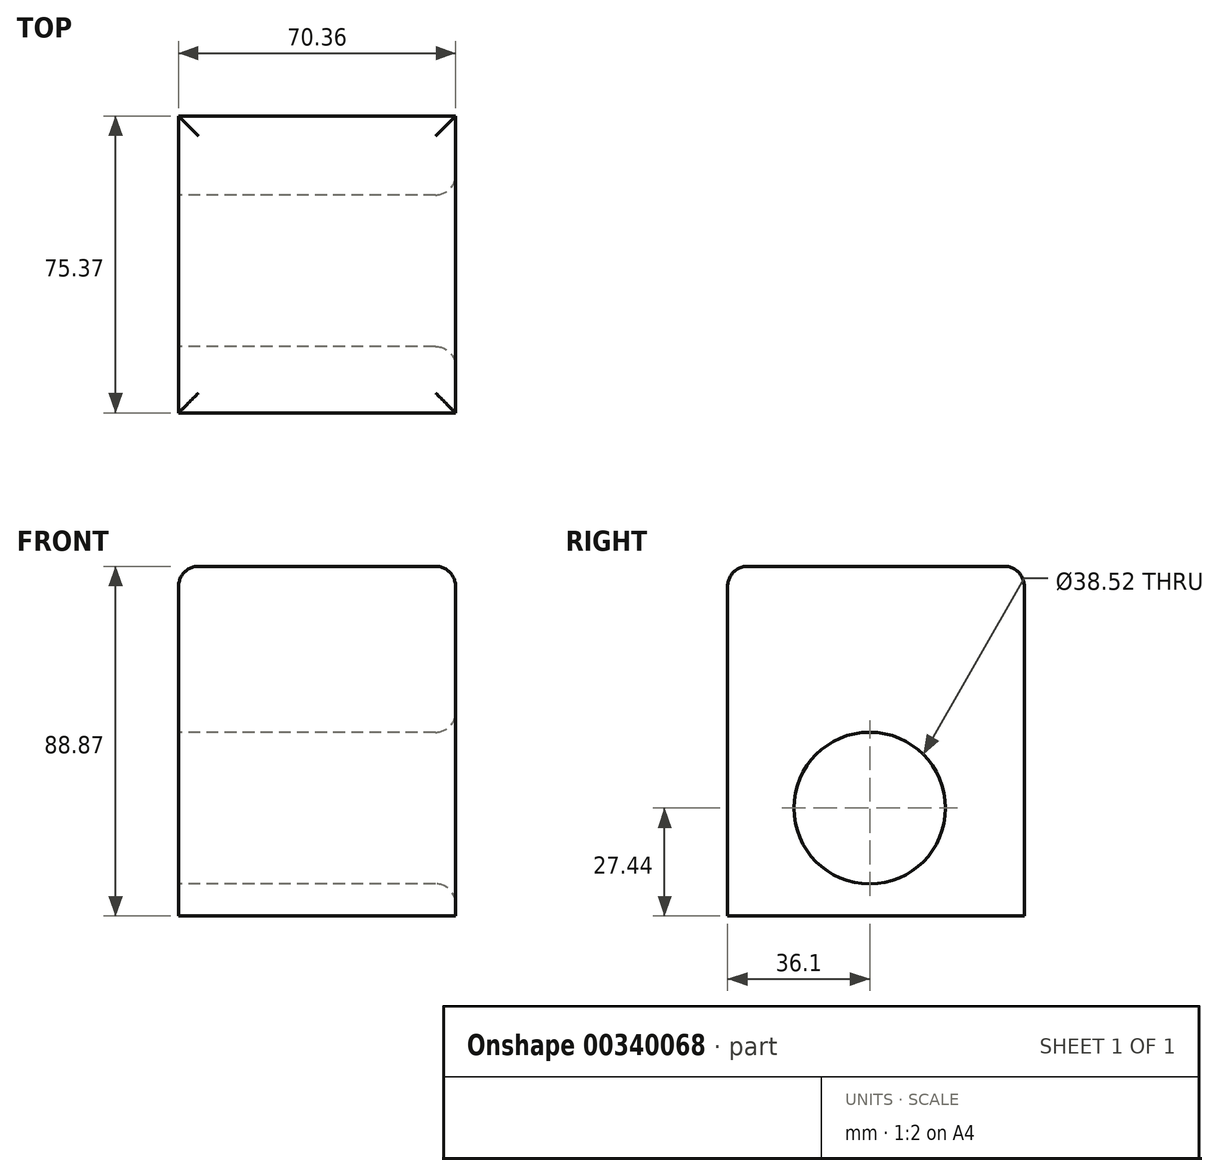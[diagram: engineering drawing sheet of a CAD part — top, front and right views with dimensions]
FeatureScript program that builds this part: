
annotation { "Feature Type Name" : "Feature", "Feature Type Description" : "" }
export const myFeature = defineFeature(function(context is Context, id is Id, definition is map)
    precondition{}
    {
        {
            var Q0;
            Q0=qCreatedBy(makeId("Right.planeOp"),FACE);
            var sketch = newSketch(context, id + "F0", { "sketchPlane" : qUnion([Q0])});
            skLineSegment(sketch, "E0.bottom", {"start": v(-36.1, 61.43) * mm, "end": v(39.27, 61.43) * mm});
            skLineSegment(sketch, "E0.top", {"start": v(-36.1, -27.44) * mm, "end": v(39.27, -27.44) * mm});
            skLineSegment(sketch, "E0.left", {"start": v(-36.1, 61.43) * mm, "end": v(-36.1, -27.44) * mm});
            skLineSegment(sketch, "E0.right", {"start": v(39.27, 61.43) * mm, "end": v(39.27, -27.44) * mm});
            skCircle(sketch, "E1", {"center": v(0, 0) * mm, "radius": 19.26 * mm});
            skSolve(sketch);
        }
        {
            var Q0;
            Q0=makeQuery(id+"F0.imprint","IMPRINT",FACE,{"disambiguationData":[TD([[makeQuery(id+"F0.imprint","IMPRINT",EDGE,{"derivedFrom":sQuery(id+"F0.wireOp",EDGE,"E0.bottom")}),-1.0]])]});
            extrude(context, id + "F1", {"entities" : qUnion([Q0]), "depth" : 70.36 * mm});
        }
        {
            var Q0;
            Q0=makeQuery(id+"F1.opExtrude","SWEPT_EDGE",EDGE,{"disambiguationData":[OSD([sQuery(id+"F0.wireOp",EDGE,"E0.bottom"),sQuery(id+"F0.wireOp",EDGE,"E0.left")])]});
            var Q1;
            Q1=makeQuery(id+"F1.opExtrude","SWEPT_EDGE",EDGE,{"disambiguationData":[OSD([sQuery(id+"F0.wireOp",EDGE,"E0.bottom"),sQuery(id+"F0.wireOp",EDGE,"E0.right")])]});
            var Q2;
            Q2=makeQuery(id+"F1.opExtrude","CAP_EDGE",EDGE,{"disambiguationData":[OSD([sQuery(id+"F0.wireOp",EDGE,"E0.bottom")])],"isStart":false});
            var Q3;
            Q3=makeQuery(id+"F1.opExtrude","CAP_EDGE",EDGE,{"disambiguationData":[OSD([sQuery(id+"F0.wireOp",EDGE,"E0.bottom")])],"isStart":true});
            var Q4;
            Q4=makeQuery(id+"F1.opExtrude","CAP_EDGE",EDGE,{"disambiguationData":[OSD([sQuery(id+"F0.wireOp",EDGE,"E1")])],"isStart":false});
            fillet(context, id + "F2", {"entities" : qUnion([Q0, Q1, Q2, Q3, Q4]), "radius" : 5.08 * mm, "tangentPropagation" : true, "allowEdgeOverflow" : false});
        }
    });
